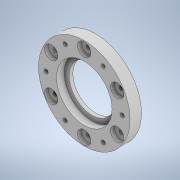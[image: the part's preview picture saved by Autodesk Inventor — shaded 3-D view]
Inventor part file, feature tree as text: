
AUTODESK INVENTOR PART (.ipt)
format: ipt  version: 2020 (Build 240168000, 168)  size: 201,216 bytes
history: native  units: in
note: dims shown in document units (in); Inventor stores cm internally (conversion verified against a paired STEP export)
features: extrude x4, sketch x4, projected_geometry x1
ambient origin geometry x8: Origin, YZ Plane, XZ Plane, XY Plane, X Axis, Y Axis, Z Axis, Center Point
bodies: Solid1 (feature_tree)
feature tree (9):
  extrude  "Extrusion1"  Depth=2.5in
  extrude  "Extrusion2"  Depth=3.0in
  extrude  "Extrusion3"  Depth=0.25in TaperAngle=0.0deg
  extrude  "Extrusion4"  Depth=0.25in
  sketch  "Sketch1"  dims[d0=2.5in d1=6.0in]
  sketch  "Sketch2"  dims[d2=0.2656in d3=3.0in]
  sketch  "Sketch3"  dims[d4=4.7244in d6=360.0deg d8=0.25in d9=0.0in]
  projected_geometry  "Projected Loop1"
  sketch  "Sketch4"  dims[d10=3.6407in d11=0.25in d12=0.5in d13=0.0in d14=0.5in d15=0.0in d16=0.875in d17=2.3622in d19=360.0deg d21=0.25in d22=0.0in]
